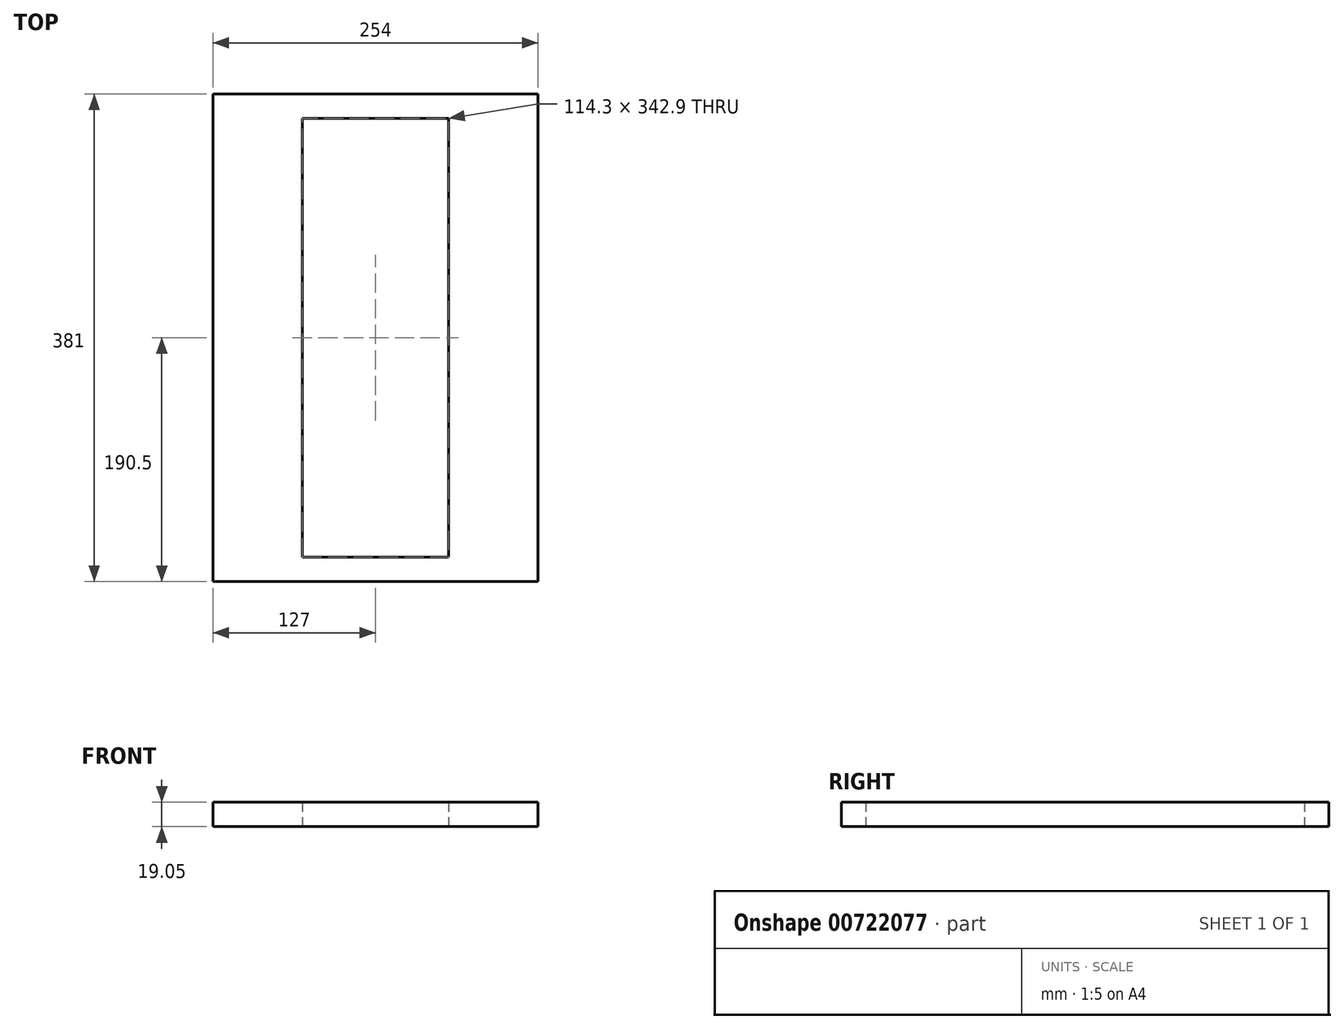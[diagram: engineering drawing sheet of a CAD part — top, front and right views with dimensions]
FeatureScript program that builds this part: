
annotation { "Feature Type Name" : "Feature", "Feature Type Description" : "" }
export const myFeature = defineFeature(function(context is Context, id is Id, definition is map)
    precondition{}
    {
        {
            var Q0;
            Q0=qCreatedBy(makeId("Top.planeOp"),FACE);
            var sketch = newSketch(context, id + "F0", { "sketchPlane" : qUnion([Q0])});
            skLineSegment(sketch, "E0.bottom", {"start": v(127, 190.5) * mm, "end": v(-127, 190.5) * mm});
            skLineSegment(sketch, "E0.top", {"start": v(127, -190.5) * mm, "end": v(-127, -190.5) * mm});
            skLineSegment(sketch, "E0.left", {"start": v(127, 190.5) * mm, "end": v(127, -190.5) * mm});
            skLineSegment(sketch, "E0.right", {"start": v(-127, 190.5) * mm, "end": v(-127, -190.5) * mm});
            skPoint(sketch, "E0.middle", {"position": v(0, 0) * mm});
            skLineSegment(sketch, "E1.bottom", {"start": v(57.15, 171.45) * mm, "end": v(-57.15, 171.45) * mm});
            skLineSegment(sketch, "E1.top", {"start": v(57.15, -171.45) * mm, "end": v(-57.15, -171.45) * mm});
            skLineSegment(sketch, "E1.left", {"start": v(57.15, 171.45) * mm, "end": v(57.15, -171.45) * mm});
            skLineSegment(sketch, "E1.right", {"start": v(-57.15, 171.45) * mm, "end": v(-57.15, -171.45) * mm});
            skSolve(sketch);
        }
        {
            var Q0;
            Q0=makeQuery(id+"F0.imprint","IMPRINT",FACE,{"disambiguationData":[TD([[makeQuery(id+"F0.imprint","IMPRINT",EDGE,{"derivedFrom":sQuery(id+"F0.wireOp",EDGE,"E0.bottom")}),1.0]])]});
            extrude(context, id + "F1", {"entities" : qUnion([Q0]), "depth" : 19.05 * mm, "offsetDistance" : 25.4 * mm});
        }
    });
